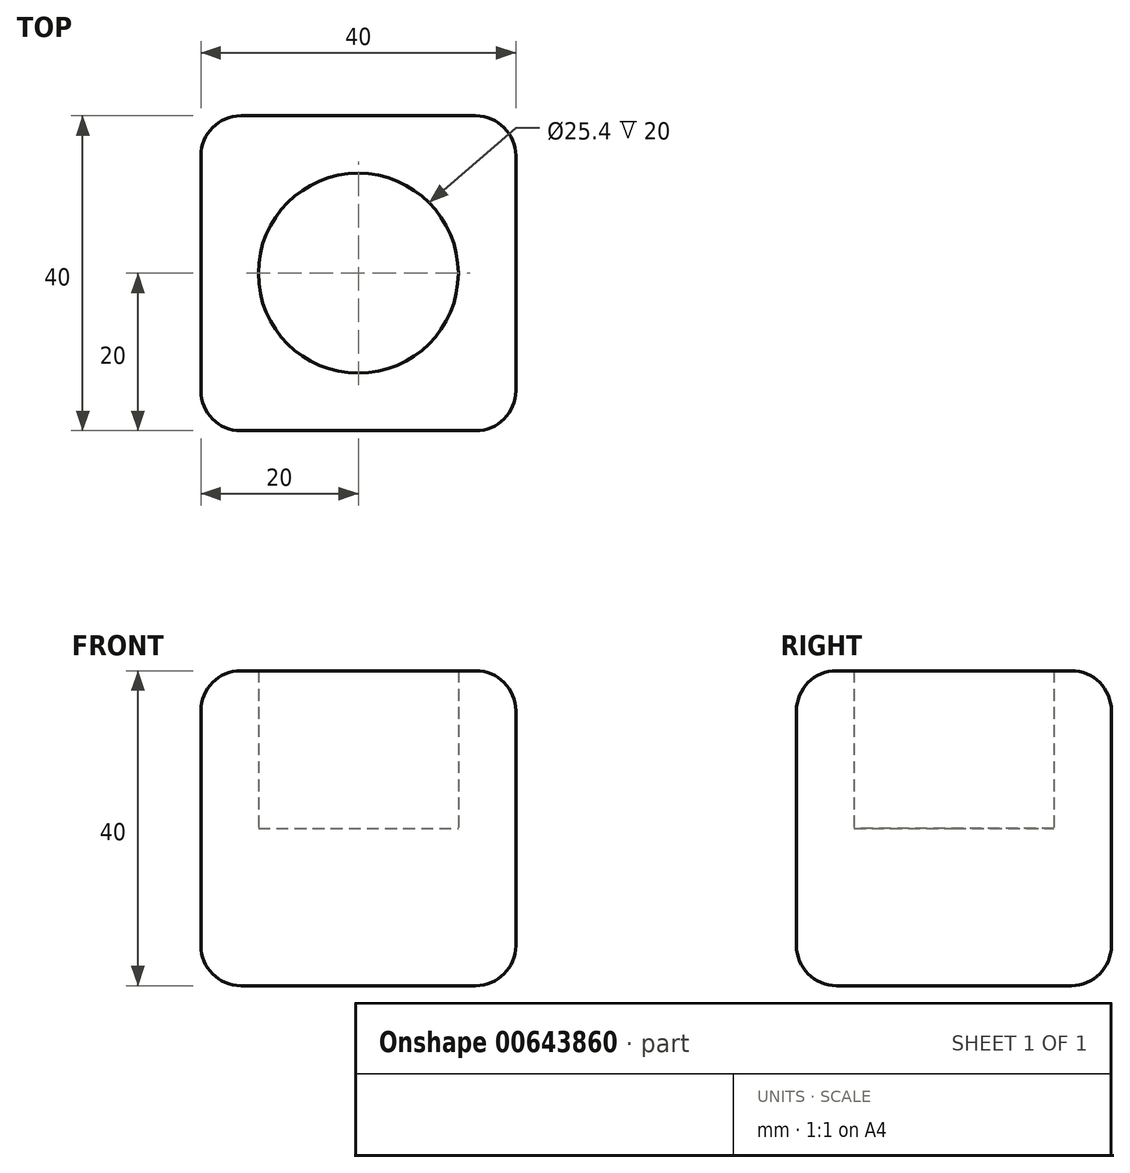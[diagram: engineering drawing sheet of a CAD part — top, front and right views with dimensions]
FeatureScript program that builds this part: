
annotation { "Feature Type Name" : "Feature", "Feature Type Description" : "" }
export const myFeature = defineFeature(function(context is Context, id is Id, definition is map)
    precondition{}
    {
        {
            var Q0;
            Q0=qCreatedBy(makeId("Top.planeOp"),FACE);
            var sketch = newSketch(context, id + "F0", { "sketchPlane" : qUnion([Q0])});
            skCircle(sketch, "E0.cCircle", {"center": v(0, 0) * mm, "radius": 20 * mm, "construction": true});
            skLineSegment(sketch, "E0.0", {"start": v(-20, 20) * mm, "end": v(20, 20) * mm});
            skLineSegment(sketch, "E0.1", {"start": v(20, 20) * mm, "end": v(20, -20) * mm});
            skLineSegment(sketch, "E0.2", {"start": v(20, -20) * mm, "end": v(-20, -20) * mm});
            skLineSegment(sketch, "E0.3", {"start": v(-20, -20) * mm, "end": v(-20, 20) * mm});
            skPoint(sketch, "E0.0.midPoint", {"position": v(0, 20) * mm});
            skSolve(sketch);
        }
        {
            var Q0;
            Q0=makeQuery(id+"F0.imprint","IMPRINT",FACE,{"disambiguationData":[TD([[makeQuery(id+"F0.imprint","IMPRINT",EDGE,{"derivedFrom":sQuery(id+"F0.wireOp",EDGE,"E0.0")}),-1.0]])]});
            extrude(context, id + "F1", {"entities" : qUnion([Q0]), "endBound" : BoundingType.SYMMETRIC, "depth" : 40 * mm, "offsetDistance" : 25.4 * mm});
        }
        {
            var Q0;
            Q0=makeQuery(id+"F1.opExtrude","CAP_EDGE",EDGE,{"disambiguationData":[OSD([sQuery(id+"F0.wireOp",EDGE,"E0.2")])],"isStart":false});
            var Q1;
            Q1=makeQuery(id+"F1.opExtrude","CAP_EDGE",EDGE,{"disambiguationData":[OSD([sQuery(id+"F0.wireOp",EDGE,"E0.1")])],"isStart":false});
            var Q2;
            Q2=makeQuery(id+"F1.opExtrude","CAP_EDGE",EDGE,{"disambiguationData":[OSD([sQuery(id+"F0.wireOp",EDGE,"E0.0")])],"isStart":false});
            var Q3;
            Q3=makeQuery(id+"F1.opExtrude","CAP_EDGE",EDGE,{"disambiguationData":[OSD([sQuery(id+"F0.wireOp",EDGE,"E0.3")])],"isStart":false});
            var Q4;
            Q4=makeQuery(id+"F1.opExtrude","SWEPT_EDGE",EDGE,{"disambiguationData":[OSD([sQuery(id+"F0.wireOp",EDGE,"E0.2"),sQuery(id+"F0.wireOp",EDGE,"E0.3")])]});
            var Q5;
            Q5=makeQuery(id+"F1.opExtrude","SWEPT_EDGE",EDGE,{"disambiguationData":[OSD([sQuery(id+"F0.wireOp",EDGE,"E0.1"),sQuery(id+"F0.wireOp",EDGE,"E0.2")])]});
            var Q6;
            Q6=makeQuery(id+"F1.opExtrude","SWEPT_FACE",FACE,{"disambiguationData":[OSD([sQuery(id+"F0.wireOp",EDGE,"E0.1")])]});
            var Q7;
            Q7=makeQuery(id+"F1.opExtrude","CAP_EDGE",EDGE,{"disambiguationData":[OSD([sQuery(id+"F0.wireOp",EDGE,"E0.2")])],"isStart":true});
            var Q8;
            Q8=makeQuery(id+"F1.opExtrude","CAP_EDGE",EDGE,{"disambiguationData":[OSD([sQuery(id+"F0.wireOp",EDGE,"E0.3")])],"isStart":true});
            var Q9;
            Q9=makeQuery(id+"F1.opExtrude","CAP_EDGE",EDGE,{"disambiguationData":[OSD([sQuery(id+"F0.wireOp",EDGE,"E0.0")])],"isStart":true});
            var Q10;
            Q10=makeQuery(id+"F1.opExtrude","SWEPT_EDGE",EDGE,{"disambiguationData":[OSD([sQuery(id+"F0.wireOp",EDGE,"E0.0"),sQuery(id+"F0.wireOp",EDGE,"E0.3")])]});
            fillet(context, id + "F2", {"entities" : qUnion([Q0, Q1, Q2, Q3, Q4, Q5, Q6, Q7, Q8, Q9, Q10]), "radius" : 5.08 * mm, "tangentPropagation" : true, "allowEdgeOverflow" : false});
        }
        {
            var Q0;
            Q0=sQuery(id+"F0.wireOp",VERTEX,"E0.cCircle.center");
            var Q1;
            Q1=makeQuery(id+"F1.opExtrude","SWEPT_BODY",BODY,{"disambiguationData":[OSD([sQuery(id+"F0.wireOp",EDGE,"E0.0"),sQuery(id+"F0.wireOp",EDGE,"E0.1"),sQuery(id+"F0.wireOp",EDGE,"E0.2"),sQuery(id+"F0.wireOp",EDGE,"E0.3")])]});
            hole(context, id + "F3", {"style" : HoleStyle.SIMPLE, "endStyle" : HoleEndStyle.THROUGH, "oppositeDirection" : true, "holeDiameter" : 25.4 * mm, "majorDiameter" : 6.35 * mm, "isTappedThrough" : true, "tappedDepth" : 12.7 * mm, "tapClearance" : 3, "locations" : qUnion([Q0]), "scope" : qUnion([Q1])});
        }
    });
